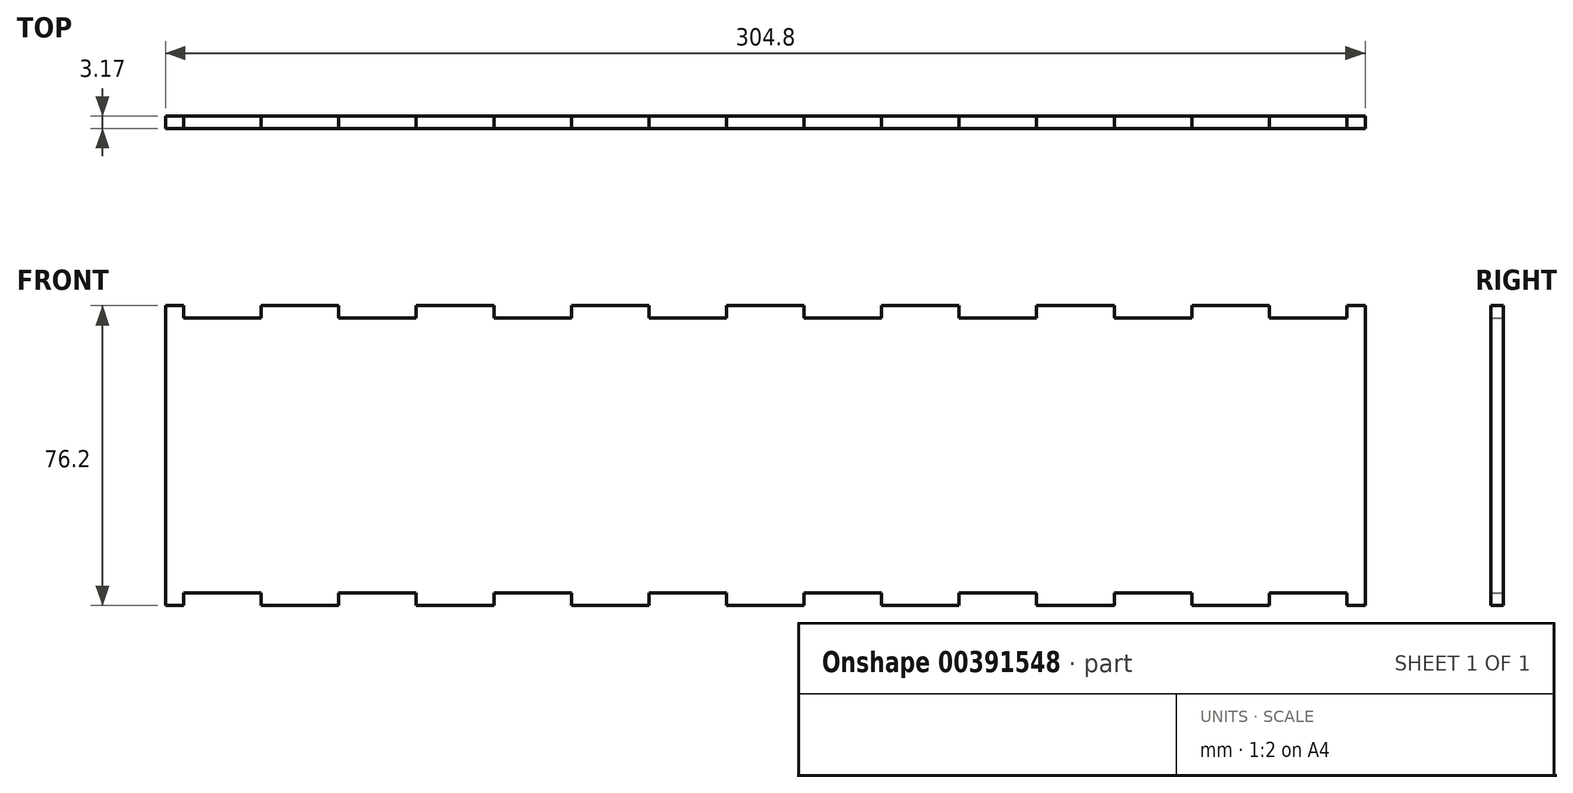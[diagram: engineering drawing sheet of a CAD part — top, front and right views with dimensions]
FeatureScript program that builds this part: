
annotation { "Feature Type Name" : "Feature", "Feature Type Description" : "" }
export const myFeature = defineFeature(function(context is Context, id is Id, definition is map)
    precondition{}
    {
        {
            var Q0;
            Q0=qCreatedBy(makeId("Front.planeOp"),FACE);
            var sketch = newSketch(context, id + "F0", { "sketchPlane" : qUnion([Q0])});
            skLineSegment(sketch, "E0.bottom", {"start": v(-384.18, -38.1) * mm, "end": v(384.17, -38.1) * mm, "construction": true});
            skLineSegment(sketch, "E0.left", {"start": v(-384.18, -38.1) * mm, "end": v(-384.18, 38.1) * mm, "construction": true});
            skPoint(sketch, "E0.middle", {"position": v(0, 0) * mm});
            skLineSegment(sketch, "E1", {"start": v(-384.18, 12.7) * mm, "end": v(-381, 12.7) * mm});
            skLineSegment(sketch, "E2", {"start": v(-381, 12.7) * mm, "end": v(-381, -12.7) * mm});
            skLineSegment(sketch, "E3", {"start": v(-381, -12.7) * mm, "end": v(-384.18, -12.7) * mm});
            skLineSegment(sketch, "E4", {"start": v(-384.18, -12.7) * mm, "end": v(-384.18, -38.1) * mm});
            skLineSegment(sketch, "E5", {"start": v(-384.18, 34.92) * mm, "end": v(-364.47, 34.92) * mm});
            skLineSegment(sketch, "E6", {"start": v(-364.47, 34.92) * mm, "end": v(-364.47, 38.1) * mm});
            skLineSegment(sketch, "E7", {"start": v(-364.47, 38.1) * mm, "end": v(-344.77, 38.1) * mm});
            skLineSegment(sketch, "E8", {"start": v(-344.77, 38.1) * mm, "end": v(-344.77, 34.93) * mm});
            skLineSegment(sketch, "E9", {"start": v(-384.18, 38.1) * mm, "end": v(384.17, 38.1) * mm, "construction": true});
            skLineSegment(sketch, "E10.1.0.0", {"start": v(-344.77, 34.92) * mm, "end": v(-325.07, 34.92) * mm});
            skLineSegment(sketch, "E10.1.0.1", {"start": v(-325.07, 34.92) * mm, "end": v(-325.07, 38.1) * mm});
            skLineSegment(sketch, "E10.1.0.2", {"start": v(-325.07, 38.1) * mm, "end": v(-305.37, 38.1) * mm});
            skLineSegment(sketch, "E10.1.0.3", {"start": v(-305.37, 38.1) * mm, "end": v(-305.37, 34.93) * mm});
            skLineSegment(sketch, "E10.2.0.0", {"start": v(-305.37, 34.92) * mm, "end": v(-285.67, 34.92) * mm});
            skLineSegment(sketch, "E10.2.0.1", {"start": v(-285.67, 34.92) * mm, "end": v(-285.67, 38.1) * mm});
            skLineSegment(sketch, "E10.2.0.2", {"start": v(-285.67, 38.1) * mm, "end": v(-265.97, 38.1) * mm});
            skLineSegment(sketch, "E10.2.0.3", {"start": v(-265.97, 38.1) * mm, "end": v(-265.97, 34.93) * mm});
            skLineSegment(sketch, "E10.3.0.0", {"start": v(-265.97, 34.92) * mm, "end": v(-246.27, 34.92) * mm});
            skLineSegment(sketch, "E10.3.0.1", {"start": v(-246.27, 34.92) * mm, "end": v(-246.27, 38.1) * mm});
            skLineSegment(sketch, "E10.3.0.2", {"start": v(-246.27, 38.1) * mm, "end": v(-226.56, 38.1) * mm});
            skLineSegment(sketch, "E10.3.0.3", {"start": v(-226.56, 38.1) * mm, "end": v(-226.56, 34.93) * mm});
            skLineSegment(sketch, "E10.4.0.0", {"start": v(-226.56, 34.92) * mm, "end": v(-206.86, 34.92) * mm});
            skLineSegment(sketch, "E10.4.0.1", {"start": v(-206.86, 34.92) * mm, "end": v(-206.86, 38.1) * mm});
            skLineSegment(sketch, "E10.4.0.2", {"start": v(-206.86, 38.1) * mm, "end": v(-187.16, 38.1) * mm});
            skLineSegment(sketch, "E10.4.0.3", {"start": v(-187.16, 38.1) * mm, "end": v(-187.16, 34.93) * mm});
            skLineSegment(sketch, "E10.5.0.0", {"start": v(-187.16, 34.92) * mm, "end": v(-167.46, 34.92) * mm});
            skLineSegment(sketch, "E10.5.0.1", {"start": v(-167.46, 34.92) * mm, "end": v(-167.46, 38.1) * mm});
            skLineSegment(sketch, "E10.5.0.2", {"start": v(-167.46, 38.1) * mm, "end": v(-147.76, 38.1) * mm});
            skLineSegment(sketch, "E10.5.0.3", {"start": v(-147.76, 38.1) * mm, "end": v(-147.76, 34.93) * mm});
            skLineSegment(sketch, "E10.6.0.0", {"start": v(-147.76, 34.92) * mm, "end": v(-128.06, 34.92) * mm});
            skLineSegment(sketch, "E10.6.0.1", {"start": v(-128.06, 34.92) * mm, "end": v(-128.06, 38.1) * mm});
            skLineSegment(sketch, "E10.6.0.2", {"start": v(-128.06, 38.1) * mm, "end": v(-108.36, 38.1) * mm});
            skLineSegment(sketch, "E10.6.0.3", {"start": v(-108.36, 38.1) * mm, "end": v(-108.36, 34.93) * mm});
            skLineSegment(sketch, "E10.7.0.0", {"start": v(-108.36, 34.92) * mm, "end": v(-88.66, 34.92) * mm});
            skLineSegment(sketch, "E10.7.0.1", {"start": v(-88.66, 34.92) * mm, "end": v(-88.66, 38.1) * mm});
            skLineSegment(sketch, "E10.7.0.2", {"start": v(-88.66, 38.1) * mm, "end": v(-68.95, 38.1) * mm});
            skLineSegment(sketch, "E10.7.0.3", {"start": v(-68.95, 38.1) * mm, "end": v(-68.95, 34.93) * mm});
            skLineSegment(sketch, "E10.8.0.0", {"start": v(-68.95, 34.92) * mm, "end": v(-49.25, 34.92) * mm});
            skLineSegment(sketch, "E10.8.0.1", {"start": v(-49.25, 34.92) * mm, "end": v(-49.25, 38.1) * mm});
            skLineSegment(sketch, "E10.8.0.2", {"start": v(-49.25, 38.1) * mm, "end": v(-29.55, 38.1) * mm});
            skLineSegment(sketch, "E10.8.0.3", {"start": v(-29.55, 38.1) * mm, "end": v(-29.55, 34.93) * mm});
            skLineSegment(sketch, "E10.9.0.0", {"start": v(-29.55, 34.92) * mm, "end": v(-9.85, 34.92) * mm});
            skLineSegment(sketch, "E10.9.0.1", {"start": v(-9.85, 34.92) * mm, "end": v(-9.85, 38.1) * mm});
            skLineSegment(sketch, "E10.9.0.2", {"start": v(-9.85, 38.1) * mm, "end": v(9.85, 38.1) * mm});
            skLineSegment(sketch, "E10.9.0.3", {"start": v(9.85, 38.1) * mm, "end": v(9.85, 34.93) * mm});
            skLineSegment(sketch, "E10.10.0.0", {"start": v(9.85, 34.92) * mm, "end": v(29.55, 34.92) * mm});
            skLineSegment(sketch, "E10.10.0.1", {"start": v(29.55, 34.92) * mm, "end": v(29.55, 38.1) * mm});
            skLineSegment(sketch, "E10.10.0.2", {"start": v(29.55, 38.1) * mm, "end": v(49.25, 38.1) * mm});
            skLineSegment(sketch, "E10.10.0.3", {"start": v(49.25, 38.1) * mm, "end": v(49.25, 34.93) * mm});
            skLineSegment(sketch, "E10.11.0.0", {"start": v(49.25, 34.92) * mm, "end": v(68.95, 34.92) * mm});
            skLineSegment(sketch, "E10.11.0.1", {"start": v(68.95, 34.92) * mm, "end": v(68.95, 38.1) * mm});
            skLineSegment(sketch, "E10.11.0.2", {"start": v(68.95, 38.1) * mm, "end": v(88.66, 38.1) * mm});
            skLineSegment(sketch, "E10.11.0.3", {"start": v(88.66, 38.1) * mm, "end": v(88.66, 34.93) * mm});
            skLineSegment(sketch, "E10.12.0.0", {"start": v(88.66, 34.92) * mm, "end": v(108.36, 34.92) * mm});
            skLineSegment(sketch, "E10.12.0.1", {"start": v(108.36, 34.92) * mm, "end": v(108.36, 38.1) * mm});
            skLineSegment(sketch, "E10.12.0.2", {"start": v(108.36, 38.1) * mm, "end": v(128.06, 38.1) * mm});
            skLineSegment(sketch, "E10.12.0.3", {"start": v(128.06, 38.1) * mm, "end": v(128.06, 34.93) * mm});
            skLineSegment(sketch, "E10.13.0.0", {"start": v(128.06, 34.92) * mm, "end": v(147.76, 34.92) * mm});
            skLineSegment(sketch, "E10.13.0.1", {"start": v(147.76, 34.92) * mm, "end": v(147.76, 38.1) * mm});
            skLineSegment(sketch, "E10.13.0.2", {"start": v(147.76, 38.1) * mm, "end": v(167.46, 38.1) * mm});
            skLineSegment(sketch, "E10.13.0.3", {"start": v(167.46, 38.1) * mm, "end": v(167.46, 34.93) * mm});
            skLineSegment(sketch, "E10.14.0.0", {"start": v(167.46, 34.92) * mm, "end": v(187.16, 34.92) * mm});
            skLineSegment(sketch, "E10.14.0.1", {"start": v(187.16, 34.92) * mm, "end": v(187.16, 38.1) * mm});
            skLineSegment(sketch, "E10.14.0.2", {"start": v(187.16, 38.1) * mm, "end": v(206.86, 38.1) * mm});
            skLineSegment(sketch, "E10.14.0.3", {"start": v(206.86, 38.1) * mm, "end": v(206.86, 34.93) * mm});
            skLineSegment(sketch, "E10.15.0.0", {"start": v(206.86, 34.92) * mm, "end": v(226.56, 34.92) * mm});
            skLineSegment(sketch, "E10.15.0.1", {"start": v(226.56, 34.92) * mm, "end": v(226.56, 38.1) * mm});
            skLineSegment(sketch, "E10.15.0.2", {"start": v(226.56, 38.1) * mm, "end": v(246.27, 38.1) * mm});
            skLineSegment(sketch, "E10.15.0.3", {"start": v(246.27, 38.1) * mm, "end": v(246.27, 34.93) * mm});
            skLineSegment(sketch, "E10.16.0.0", {"start": v(246.27, 34.92) * mm, "end": v(265.97, 34.92) * mm});
            skLineSegment(sketch, "E10.16.0.1", {"start": v(265.97, 34.92) * mm, "end": v(265.97, 38.1) * mm});
            skLineSegment(sketch, "E10.16.0.2", {"start": v(265.97, 38.1) * mm, "end": v(285.67, 38.1) * mm});
            skLineSegment(sketch, "E10.16.0.3", {"start": v(285.67, 38.1) * mm, "end": v(285.67, 34.93) * mm});
            skLineSegment(sketch, "E10.17.0.0", {"start": v(285.67, 34.92) * mm, "end": v(305.37, 34.92) * mm});
            skLineSegment(sketch, "E10.17.0.1", {"start": v(305.37, 34.92) * mm, "end": v(305.37, 38.1) * mm});
            skLineSegment(sketch, "E10.17.0.2", {"start": v(305.37, 38.1) * mm, "end": v(325.07, 38.1) * mm});
            skLineSegment(sketch, "E10.17.0.3", {"start": v(325.07, 38.1) * mm, "end": v(325.07, 34.93) * mm});
            skLineSegment(sketch, "E10.18.0.0", {"start": v(325.07, 34.92) * mm, "end": v(344.77, 34.92) * mm});
            skLineSegment(sketch, "E10.18.0.1", {"start": v(344.77, 34.92) * mm, "end": v(344.77, 38.1) * mm});
            skLineSegment(sketch, "E10.18.0.2", {"start": v(344.77, 38.1) * mm, "end": v(364.47, 38.1) * mm});
            skLineSegment(sketch, "E10.18.0.3", {"start": v(364.47, 38.1) * mm, "end": v(364.47, 34.93) * mm});
            skLineSegment(sketch, "E10.19.0.0", {"start": v(364.47, 34.92) * mm, "end": v(384.18, 34.92) * mm});
            skLineSegment(sketch, "E10.direction1", {"start": v(-384.18, 34.92) * mm, "end": v(-344.77, 34.92) * mm, "construction": true});
            skLineSegment(sketch, "E11", {"start": v(-384.18, 34.92) * mm, "end": v(-384.18, 12.7) * mm});
            skLineSegment(sketch, "E12.MirrorCS", {"start": v(-364.47, -34.92) * mm, "end": v(-364.47, -38.1) * mm});
            skLineSegment(sketch, "E13.MirrorCS", {"start": v(-265.97, -38.1) * mm, "end": v(-265.97, -34.93) * mm});
            skLineSegment(sketch, "E14.MirrorCS", {"start": v(364.47, -38.1) * mm, "end": v(364.47, -34.93) * mm});
            skLineSegment(sketch, "E15.MirrorCS", {"start": v(206.86, -38.1) * mm, "end": v(206.86, -34.93) * mm});
            skLineSegment(sketch, "E16.MirrorCS", {"start": v(49.25, -38.1) * mm, "end": v(49.25, -34.93) * mm});
            skLineSegment(sketch, "E17.MirrorCS", {"start": v(-108.36, -38.1) * mm, "end": v(-108.36, -34.93) * mm});
            skLineSegment(sketch, "E18.MirrorCS", {"start": v(-325.07, -34.92) * mm, "end": v(-325.07, -38.1) * mm});
            skLineSegment(sketch, "E19.MirrorCS", {"start": v(-344.77, -38.1) * mm, "end": v(-344.77, -34.93) * mm});
            skLineSegment(sketch, "E20.MirrorCS", {"start": v(128.06, -38.1) * mm, "end": v(128.06, -34.93) * mm});
            skLineSegment(sketch, "E21.MirrorCS", {"start": v(-29.55, -38.1) * mm, "end": v(-29.55, -34.93) * mm});
            skLineSegment(sketch, "E22.MirrorCS", {"start": v(-187.16, -38.1) * mm, "end": v(-187.16, -34.93) * mm});
            skLineSegment(sketch, "E23.MirrorCS", {"start": v(285.67, -38.1) * mm, "end": v(285.67, -34.93) * mm});
            skLineSegment(sketch, "E24.MirrorCS", {"start": v(305.37, -34.92) * mm, "end": v(305.37, -38.1) * mm});
            skLineSegment(sketch, "E25.MirrorCS", {"start": v(147.76, -34.92) * mm, "end": v(147.76, -38.1) * mm});
            skLineSegment(sketch, "E26.MirrorCS", {"start": v(-9.85, -34.92) * mm, "end": v(-9.85, -38.1) * mm});
            skLineSegment(sketch, "E27.MirrorCS", {"start": v(-167.46, -34.92) * mm, "end": v(-167.46, -38.1) * mm});
            skLineSegment(sketch, "E28.MirrorCS", {"start": v(-246.27, -34.92) * mm, "end": v(-246.27, -38.1) * mm});
            skLineSegment(sketch, "E29.MirrorCS", {"start": v(226.56, -34.92) * mm, "end": v(226.56, -38.1) * mm});
            skLineSegment(sketch, "E30.MirrorCS", {"start": v(68.95, -34.92) * mm, "end": v(68.95, -38.1) * mm});
            skLineSegment(sketch, "E31.MirrorCS", {"start": v(-88.66, -34.92) * mm, "end": v(-88.66, -38.1) * mm});
            skLineSegment(sketch, "E32.MirrorCS", {"start": v(-305.37, -38.1) * mm, "end": v(-305.37, -34.93) * mm});
            skLineSegment(sketch, "E33.MirrorCS", {"start": v(88.66, -38.1) * mm, "end": v(88.66, -34.93) * mm});
            skLineSegment(sketch, "E34.MirrorCS", {"start": v(-68.95, -38.1) * mm, "end": v(-68.95, -34.93) * mm});
            skLineSegment(sketch, "E35.MirrorCS", {"start": v(-226.56, -38.1) * mm, "end": v(-226.56, -34.93) * mm});
            skLineSegment(sketch, "E36.MirrorCS", {"start": v(246.27, -38.1) * mm, "end": v(246.27, -34.93) * mm});
            skLineSegment(sketch, "E37.MirrorCS", {"start": v(-285.67, -34.92) * mm, "end": v(-285.67, -38.1) * mm});
            skLineSegment(sketch, "E38.MirrorCS", {"start": v(344.77, -34.92) * mm, "end": v(344.77, -38.1) * mm});
            skLineSegment(sketch, "E39.MirrorCS", {"start": v(187.16, -34.92) * mm, "end": v(187.16, -38.1) * mm});
            skLineSegment(sketch, "E40.MirrorCS", {"start": v(29.55, -34.92) * mm, "end": v(29.55, -38.1) * mm});
            skLineSegment(sketch, "E41.MirrorCS", {"start": v(-128.06, -34.92) * mm, "end": v(-128.06, -38.1) * mm});
            skLineSegment(sketch, "E42.MirrorCS", {"start": v(-49.25, -34.92) * mm, "end": v(-49.25, -38.1) * mm});
            skLineSegment(sketch, "E43.MirrorCS", {"start": v(108.36, -34.92) * mm, "end": v(108.36, -38.1) * mm});
            skLineSegment(sketch, "E44.MirrorCS", {"start": v(-206.86, -34.92) * mm, "end": v(-206.86, -38.1) * mm});
            skLineSegment(sketch, "E45.MirrorCS", {"start": v(265.97, -34.92) * mm, "end": v(265.97, -38.1) * mm});
            skLineSegment(sketch, "E46.MirrorCS", {"start": v(325.07, -38.1) * mm, "end": v(325.07, -34.93) * mm});
            skLineSegment(sketch, "E47.MirrorCS", {"start": v(9.85, -38.1) * mm, "end": v(9.85, -34.93) * mm});
            skLineSegment(sketch, "E48.MirrorCS", {"start": v(167.46, -38.1) * mm, "end": v(167.46, -34.93) * mm});
            skLineSegment(sketch, "E49.MirrorCS", {"start": v(-147.76, -38.1) * mm, "end": v(-147.76, -34.93) * mm});
            skLineSegment(sketch, "E50.MirrorCS", {"start": v(108.36, -38.1) * mm, "end": v(128.06, -38.1) * mm});
            skLineSegment(sketch, "E51.MirrorCS", {"start": v(-49.25, -38.1) * mm, "end": v(-29.55, -38.1) * mm});
            skLineSegment(sketch, "E52.MirrorCS", {"start": v(-206.86, -38.1) * mm, "end": v(-187.16, -38.1) * mm});
            skLineSegment(sketch, "E53.MirrorCS", {"start": v(265.97, -38.1) * mm, "end": v(285.67, -38.1) * mm});
            skLineSegment(sketch, "E54.MirrorCS", {"start": v(-325.07, -38.1) * mm, "end": v(-305.37, -38.1) * mm});
            skLineSegment(sketch, "E55.MirrorCS", {"start": v(-384.18, -34.92) * mm, "end": v(-364.47, -34.92) * mm});
            skLineSegment(sketch, "E56.MirrorCS", {"start": v(-364.47, -38.1) * mm, "end": v(-344.77, -38.1) * mm});
            skLineSegment(sketch, "E57.MirrorCS", {"start": v(305.37, -38.1) * mm, "end": v(325.07, -38.1) * mm});
            skLineSegment(sketch, "E58.MirrorCS", {"start": v(147.76, -38.1) * mm, "end": v(167.46, -38.1) * mm});
            skLineSegment(sketch, "E59.MirrorCS", {"start": v(-9.85, -38.1) * mm, "end": v(9.85, -38.1) * mm});
            skLineSegment(sketch, "E60.MirrorCS", {"start": v(-167.46, -38.1) * mm, "end": v(-147.76, -38.1) * mm});
            skLineSegment(sketch, "E61.MirrorCS", {"start": v(-246.27, -38.1) * mm, "end": v(-226.56, -38.1) * mm});
            skLineSegment(sketch, "E62.MirrorCS", {"start": v(226.56, -38.1) * mm, "end": v(246.27, -38.1) * mm});
            skLineSegment(sketch, "E63.MirrorCS", {"start": v(68.95, -38.1) * mm, "end": v(88.66, -38.1) * mm});
            skLineSegment(sketch, "E64.MirrorCS", {"start": v(-88.66, -38.1) * mm, "end": v(-68.95, -38.1) * mm});
            skLineSegment(sketch, "E65.MirrorCS", {"start": v(-285.67, -38.1) * mm, "end": v(-265.97, -38.1) * mm});
            skLineSegment(sketch, "E66.MirrorCS", {"start": v(344.77, -38.1) * mm, "end": v(364.47, -38.1) * mm});
            skLineSegment(sketch, "E67.MirrorCS", {"start": v(187.16, -38.1) * mm, "end": v(206.86, -38.1) * mm});
            skLineSegment(sketch, "E68.MirrorCS", {"start": v(29.55, -38.1) * mm, "end": v(49.25, -38.1) * mm});
            skLineSegment(sketch, "E69.MirrorCS", {"start": v(-128.06, -38.1) * mm, "end": v(-108.36, -38.1) * mm});
            skLineSegment(sketch, "E70.MirrorCS", {"start": v(-344.77, -34.92) * mm, "end": v(-325.07, -34.92) * mm});
            skLineSegment(sketch, "E71.MirrorCS", {"start": v(-265.97, -34.92) * mm, "end": v(-246.27, -34.92) * mm});
            skLineSegment(sketch, "E72.MirrorCS", {"start": v(364.47, -34.92) * mm, "end": v(384.18, -34.92) * mm});
            skLineSegment(sketch, "E73.MirrorCS", {"start": v(206.86, -34.92) * mm, "end": v(226.56, -34.92) * mm});
            skLineSegment(sketch, "E74.MirrorCS", {"start": v(49.25, -34.92) * mm, "end": v(68.95, -34.92) * mm});
            skLineSegment(sketch, "E75.MirrorCS", {"start": v(-108.36, -34.92) * mm, "end": v(-88.66, -34.92) * mm});
            skLineSegment(sketch, "E76.MirrorCS", {"start": v(-305.37, -34.92) * mm, "end": v(-285.67, -34.92) * mm});
            skLineSegment(sketch, "E77.MirrorCS", {"start": v(325.07, -34.92) * mm, "end": v(344.77, -34.92) * mm});
            skLineSegment(sketch, "E78.MirrorCS", {"start": v(167.46, -34.92) * mm, "end": v(187.16, -34.92) * mm});
            skLineSegment(sketch, "E79.MirrorCS", {"start": v(9.85, -34.92) * mm, "end": v(29.55, -34.92) * mm});
            skLineSegment(sketch, "E80.MirrorCS", {"start": v(-147.76, -34.92) * mm, "end": v(-128.06, -34.92) * mm});
            skLineSegment(sketch, "E81.MirrorCS", {"start": v(128.06, -34.92) * mm, "end": v(147.76, -34.92) * mm});
            skLineSegment(sketch, "E82.MirrorCS", {"start": v(-29.55, -34.92) * mm, "end": v(-9.85, -34.92) * mm});
            skLineSegment(sketch, "E83.MirrorCS", {"start": v(-187.16, -34.92) * mm, "end": v(-167.46, -34.92) * mm});
            skLineSegment(sketch, "E84.MirrorCS", {"start": v(285.67, -34.92) * mm, "end": v(305.37, -34.92) * mm});
            skLineSegment(sketch, "E85.MirrorCS", {"start": v(88.66, -34.92) * mm, "end": v(108.36, -34.92) * mm});
            skLineSegment(sketch, "E86.MirrorCS", {"start": v(-68.95, -34.92) * mm, "end": v(-49.25, -34.92) * mm});
            skLineSegment(sketch, "E87.MirrorCS", {"start": v(-226.56, -34.92) * mm, "end": v(-206.86, -34.92) * mm});
            skLineSegment(sketch, "E88.MirrorCS", {"start": v(246.27, -34.92) * mm, "end": v(265.97, -34.92) * mm});
            skLineSegment(sketch, "E89.MirrorCS", {"start": v(-384.18, -34.92) * mm, "end": v(-344.77, -34.92) * mm, "construction": true});
            skLineSegment(sketch, "E90.MirrorCS", {"start": v(384.18, 12.7) * mm, "end": v(381, 12.7) * mm});
            skLineSegment(sketch, "E91.MirrorCS", {"start": v(381, -12.7) * mm, "end": v(384.18, -12.7) * mm});
            skLineSegment(sketch, "E92.MirrorCS", {"start": v(384.18, 34.92) * mm, "end": v(384.18, 12.7) * mm});
            skLineSegment(sketch, "E93.MirrorCS", {"start": v(384.18, -12.7) * mm, "end": v(384.18, -38.1) * mm});
            skLineSegment(sketch, "E94.MirrorCS", {"start": v(384.18, -38.1) * mm, "end": v(384.18, 38.1) * mm, "construction": true});
            skLineSegment(sketch, "E95.MirrorCS", {"start": v(381, 12.7) * mm, "end": v(381, -12.7) * mm});
            skLineSegment(sketch, "E96", {"start": v(-152.4, 103.96) * mm, "end": v(-152.4, -103.36) * mm, "construction": true});
            skLineSegment(sketch, "E97", {"start": v(152.4, -103.75) * mm, "end": v(152.4, 100.9) * mm, "construction": true});
            skLineSegment(sketch, "E98", {"start": v(-152.4, 38.1) * mm, "end": v(-152.4, -38.1) * mm});
            skLineSegment(sketch, "E99", {"start": v(152.4, 38.1) * mm, "end": v(152.4, -38.1) * mm});
            skSolve(sketch);
        }
        {
            var Q0;
            {var subQ5=sQuery(id+"F0.wireOp",EDGE,"E10.5.0.3");Q0=makeQuery(id+"F0.imprint","IMPRINT",FACE,{"disambiguationData":[TD([[makeQuery(id+"F0.imprint","IMPRINT",EDGE,{"derivedFrom":subQ5}),-1.0]])]});}
            extrude(context, id + "F1", {"entities" : qUnion([Q0]), "depth" : 3.17 * mm});
        }
    });
